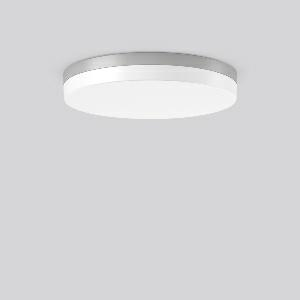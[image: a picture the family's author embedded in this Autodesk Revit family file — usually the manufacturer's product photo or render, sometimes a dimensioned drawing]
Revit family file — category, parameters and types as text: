
# Revit family: flat_slim_round_312633_004_76_c3f5
name_source: partatom
category: Lighting Fixtures
units: mm (PartAtom-declared; Revit-internal decimal feet)

## family parameters
Cut with Voids When Loaded = No
Host = Face
Light Source = No
Part Type = Normal
Room Calculation Point = No
Round Connector Dimension = Use Diameter
Shared = No

## types (1)
- MultiLumen 1 830 (1 x LED Modul 830, 3350 lm, 3000)
    Apparent Load = 31 VA
    CIE Flux Codes = 41 71 90 86 100
    Color Rendering = 80
    Color Temperature = 3000
    Default Elevation = 1800 mm
    Height = 75 mm
    Lamp = 1 x LED Modul 830
    Lamp Light Flux = 3350 lm
    Lamp count = 1
    Length = 480 mm
    Lifetime = 50000 h
    Luminous efficacy = 108 lm/W
    Manufacturer = RZB
    ModVariant = No
    Model = 312633.004.76
    Mounting Place = Ceiling
    Mounting Type = Surface mounted
    Number of Poles = 1
    OnlyDefault = Yes
    Power Factor = 1
    Product Name = FLAT SLIM round
    Product group = Surface mounted ceiling and wall luminaires
    ProductGroupID = 305
    Protection Class = Protection class I
    Protection Degree = Degree of protection
    RLX_Detail_Level = 1
    RLX_Emergency_Light_Flux = 0 lm
    RLX_Emergency_Type = 0
    RLX_Emergency_Type_DB = No
    RlxData = <blob elided: 21705 chars, md5=8eb46f45>
    Socket = socket
    Standby Power = 0 W
    System Light Flux = 3350 lm
    System Power = 31 W
    Type Comments = MultiLumen 1 830
    Type Image = 312633.004.jpg
    URL = http://relux.com
    VarID = multilumen_1_830
    Voltage = 0 V
    Weight = 0.00 kg
    Width = 0 mm  [stored 0 ft]

note: [stored X ft] marks values corroborated as IEEE doubles in the binary element streams (Revit-internal decimal feet)

## geometry (parser evidence)
native form markers: Blend x4, Sweep x14
no freeform markers — native parametric forms only
